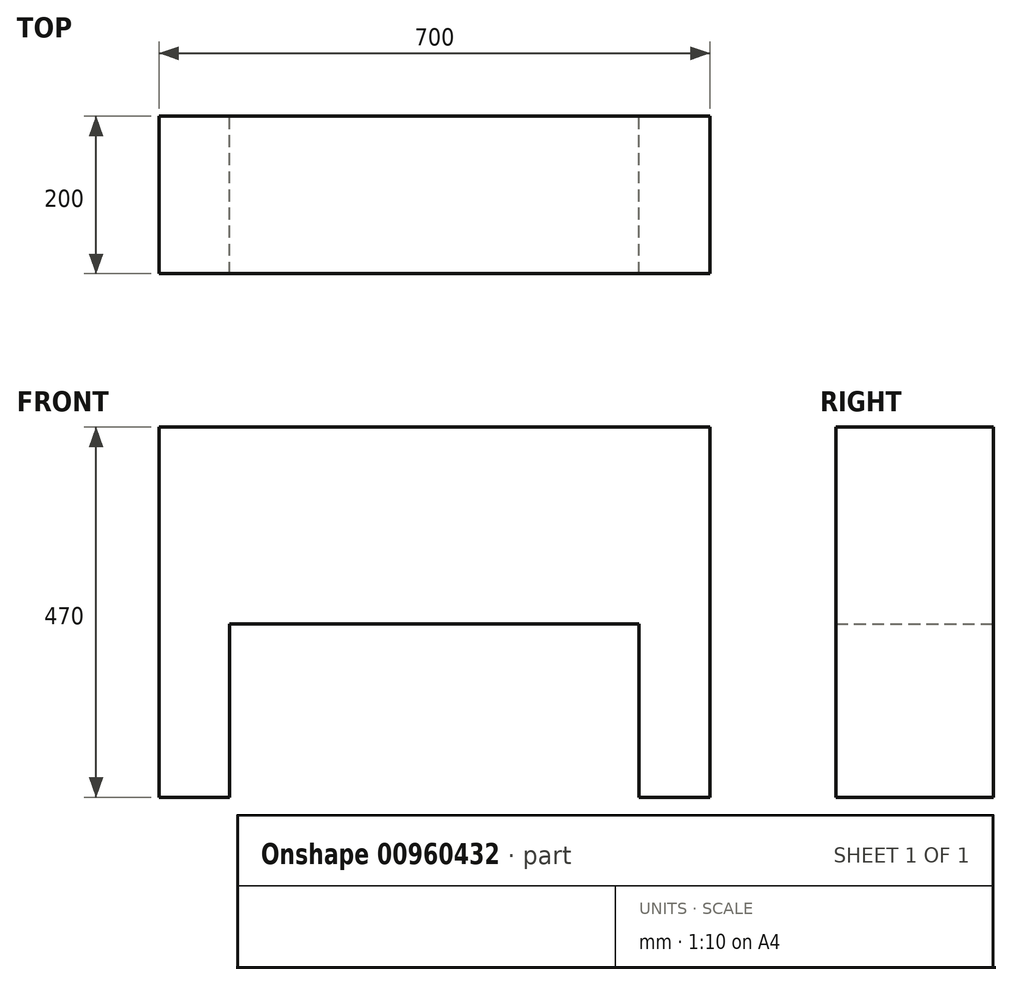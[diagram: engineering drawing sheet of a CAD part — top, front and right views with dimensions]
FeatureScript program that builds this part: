
annotation { "Feature Type Name" : "Feature", "Feature Type Description" : "" }
export const myFeature = defineFeature(function(context is Context, id is Id, definition is map)
    precondition{}
    {
        {
            var Q0;
            Q0=qCreatedBy(makeId("Front.planeOp"),FACE);
            var sketch = newSketch(context, id + "F0", { "sketchPlane" : qUnion([Q0])});
            skLineSegment(sketch, "E0.bottom", {"start": v(350, 470) * mm, "end": v(-350, 470) * mm});
            skLineSegment(sketch, "E0.left", {"start": v(350, 470) * mm, "end": v(350, 0) * mm});
            skLineSegment(sketch, "E0.right", {"start": v(-350, 470) * mm, "end": v(-350, 0) * mm});
            skPoint(sketch, "E0.middle", {"position": v(0, 0) * mm});
            skLineSegment(sketch, "E1.bottom", {"start": v(260, 220) * mm, "end": v(-260, 220) * mm});
            skLineSegment(sketch, "E1.left", {"start": v(260, 220) * mm, "end": v(260, 0) * mm});
            skLineSegment(sketch, "E1.right", {"start": v(-260, 220) * mm, "end": v(-260, 0) * mm});
            skLineSegment(sketch, "E2", {"start": v(-350, 0) * mm, "end": v(-260, 0) * mm});
            skLineSegment(sketch, "E3", {"start": v(0, -106.47) * mm, "end": v(0, 353.97) * mm, "construction": true});
            skLineSegment(sketch, "E4.trimOffspring", {"start": v(260, 0) * mm, "end": v(350, 0) * mm});
            skSolve(sketch);
        }
        {
            var Q0;
            Q0 = qSketchRegion(id + "F0", true);
            extrude(context, id + "F1", {"entities" : qUnion([Q0]), "depth" : 200 * mm, "offsetDistance" : 25 * mm});
        }
    });
